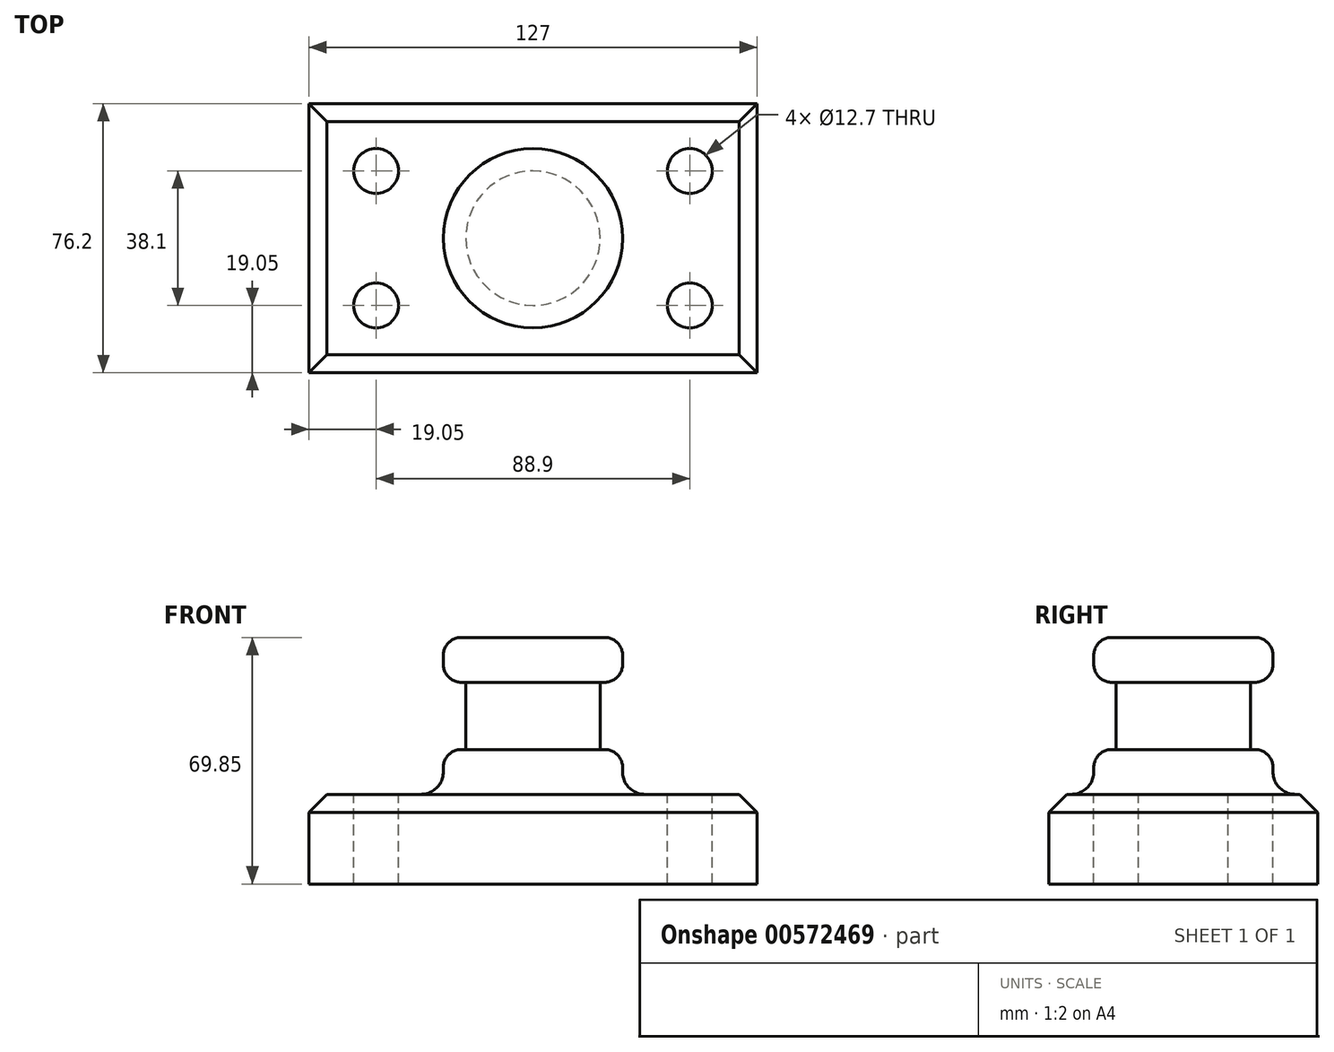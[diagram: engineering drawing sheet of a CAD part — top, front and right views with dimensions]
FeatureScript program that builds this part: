
annotation { "Feature Type Name" : "Feature", "Feature Type Description" : "" }
export const myFeature = defineFeature(function(context is Context, id is Id, definition is map)
    precondition{}
    {
        {
            var Q0;
            Q0=qCreatedBy(makeId("Top.planeOp"),FACE);
            var sketch = newSketch(context, id + "F0", { "sketchPlane" : qUnion([Q0])});
            skLineSegment(sketch, "E0.bottom", {"start": v(-63.5, 38.1) * mm, "end": v(63.5, 38.1) * mm});
            skLineSegment(sketch, "E0.top", {"start": v(-63.5, -38.1) * mm, "end": v(63.5, -38.1) * mm});
            skLineSegment(sketch, "E0.left", {"start": v(-63.5, 38.1) * mm, "end": v(-63.5, -38.1) * mm});
            skLineSegment(sketch, "E0.right", {"start": v(63.5, 38.1) * mm, "end": v(63.5, -38.1) * mm});
            skPoint(sketch, "E0.middle", {"position": v(0, 0) * mm});
            skLineSegment(sketch, "E1.bottom", {"start": v(-63.05, 38.1) * mm, "end": v(-63.76, 38.1) * mm});
            skLineSegment(sketch, "E1.top", {"start": v(-63.05, 38.1) * mm, "end": v(-63.76, 38.1) * mm});
            skLineSegment(sketch, "E1.left", {"start": v(-63.05, 38.1) * mm, "end": v(-63.05, 38.1) * mm});
            skLineSegment(sketch, "E1.right", {"start": v(-63.76, 38.1) * mm, "end": v(-63.76, 38.1) * mm});
            skPoint(sketch, "E1.middle", {"position": v(-63.4, 38.1) * mm});
            skSolve(sketch);
        }
        {
            var Q0;
            {var subQ1=sQuery(id+"F0.wireOp",EDGE,"E0.bottom");Q0=makeQuery(id+"F0.imprint","IMPRINT",FACE,{"disambiguationData":[TD([[makeQuery(id+"F0.imprint","IMPRINT",EDGE,{"derivedFrom":subQ1}),-1.0]])]});}
            extrude(context, id + "F1", {"entities" : qUnion([Q0]), "depth" : 25.4 * mm, "offsetDistance" : 25.4 * mm});
        }
        {
            var Q0;
            Q0=makeQuery(id+"F1.opExtrude","CAP_FACE",FACE,{"disambiguationData":[OSD([sQuery(id+"F0.wireOp",EDGE,"E0.bottom"),sQuery(id+"F0.wireOp",EDGE,"E0.top"),sQuery(id+"F0.wireOp",EDGE,"E0.left"),sQuery(id+"F0.wireOp",EDGE,"E0.right"),sQuery(id+"F0.wireOp",EDGE,"E1.top")])],"isStart":false});
            var sketch = newSketch(context, id + "F2", { "sketchPlane" : qUnion([Q0])});
            skCircle(sketch, "E2", {"center": v(-44.45, 19.05) * mm, "radius": 6.35 * mm});
            skCircle(sketch, "E3", {"center": v(-44.45, -19.05) * mm, "radius": 6.35 * mm});
            skCircle(sketch, "E4", {"center": v(44.45, 19.05) * mm, "radius": 6.35 * mm});
            skCircle(sketch, "E5", {"center": v(44.45, -19.05) * mm, "radius": 6.35 * mm});
            skSolve(sketch);
        }
        {
            var Q0;
            Q0=makeQuery(id+"F2.imprint","IMPRINT",FACE,{"disambiguationData":[TD([[makeQuery(id+"F2.imprint","IMPRINT",EDGE,{"derivedFrom":sQuery(id+"F2.wireOp",EDGE,"E2")}),1.0]])]});
            var Q1;
            Q1=makeQuery(id+"F2.imprint","IMPRINT",FACE,{"disambiguationData":[TD([[makeQuery(id+"F2.imprint","IMPRINT",EDGE,{"derivedFrom":sQuery(id+"F2.wireOp",EDGE,"E3")}),1.0]])]});
            var Q2;
            Q2=makeQuery(id+"F2.imprint","IMPRINT",FACE,{"disambiguationData":[TD([[makeQuery(id+"F2.imprint","IMPRINT",EDGE,{"derivedFrom":sQuery(id+"F2.wireOp",EDGE,"E4")}),1.0]])]});
            var Q3;
            Q3=makeQuery(id+"F2.imprint","IMPRINT",FACE,{"disambiguationData":[TD([[makeQuery(id+"F2.imprint","IMPRINT",EDGE,{"derivedFrom":sQuery(id+"F2.wireOp",EDGE,"E5")}),1.0]])]});
            extrude(context, id + "F3", {"entities" : qUnion([Q0, Q1, Q2, Q3]), "operationType" : NewBodyOperationType.REMOVE, "oppositeDirection" : true, "depth" : 25.4 * mm, "offsetDistance" : 25.4 * mm});
        }
        {
            var Q0;
            Q0=qCreatedBy(makeId("Front.planeOp"),FACE);
            var sketch = newSketch(context, id + "F4", { "sketchPlane" : qUnion([Q0])});
            skLineSegment(sketch, "E6.bottom", {"start": v(0, 26.27) * mm, "end": v(0, 26.27) * mm});
            skLineSegment(sketch, "E7.bottom", {"start": v(0, 38.1) * mm, "end": v(25.4, 38.1) * mm});
            skLineSegment(sketch, "E7.top", {"start": v(0, 25.4) * mm, "end": v(25.4, 25.4) * mm});
            skLineSegment(sketch, "E7.left", {"start": v(0, 38.1) * mm, "end": v(0, 25.4) * mm});
            skLineSegment(sketch, "E7.right", {"start": v(25.4, 38.1) * mm, "end": v(25.4, 25.4) * mm});
            skSolve(sketch);
        }
        {
            var Q0;
            Q0=makeQuery(id+"F4.imprint","IMPRINT",FACE,{"disambiguationData":[TD([[makeQuery(id+"F4.imprint","IMPRINT",EDGE,{"derivedFrom":sQuery(id+"F4.wireOp",EDGE,"E7.bottom")}),-1.0]])]});
            var Q1;
            Q1=sQuery(id+"F4.wireOp",EDGE,"E7.left");
            revolve(context, id + "F5", {"operationType" : NewBodyOperationType.ADD, "entities" : qUnion([Q0]), "axis" : qUnion([Q1]), "revolveType" : RevolveType.FULL});
        }
        {
            var Q0;
            Q0=qCreatedBy(makeId("Front.planeOp"),FACE);
            var sketch = newSketch(context, id + "F6", { "sketchPlane" : qUnion([Q0])});
            skLineSegment(sketch, "E8.bottom", {"start": v(0, 38.1) * mm, "end": v(19.05, 38.1) * mm});
            skLineSegment(sketch, "E8.top", {"start": v(0, 57.15) * mm, "end": v(19.05, 57.15) * mm});
            skLineSegment(sketch, "E8.left", {"start": v(0, 38.1) * mm, "end": v(0, 57.15) * mm});
            skLineSegment(sketch, "E8.right", {"start": v(19.05, 38.1) * mm, "end": v(19.05, 57.15) * mm});
            skSolve(sketch);
        }
        {
            var Q0;
            Q0=makeQuery(id+"F6.imprint","IMPRINT",FACE,{"disambiguationData":[TD([[makeQuery(id+"F6.imprint","IMPRINT",EDGE,{"derivedFrom":sQuery(id+"F6.wireOp",EDGE,"E8.bottom")}),1.0]])]});
            var Q1;
            Q1=sQuery(id+"F6.wireOp",EDGE,"E8.left");
            revolve(context, id + "F7", {"operationType" : NewBodyOperationType.ADD, "entities" : qUnion([Q0]), "axis" : qUnion([Q1]), "revolveType" : RevolveType.FULL});
        }
        {
            var Q0;
            Q0=qCreatedBy(makeId("Front.planeOp"),FACE);
            var sketch = newSketch(context, id + "F8", { "sketchPlane" : qUnion([Q0])});
            skLineSegment(sketch, "E9.bottom", {"start": v(0, 57.15) * mm, "end": v(25.4, 57.15) * mm});
            skLineSegment(sketch, "E9.top", {"start": v(0, 69.85) * mm, "end": v(25.4, 69.85) * mm});
            skLineSegment(sketch, "E9.left", {"start": v(0, 57.15) * mm, "end": v(0, 69.85) * mm});
            skLineSegment(sketch, "E9.right", {"start": v(25.4, 57.15) * mm, "end": v(25.4, 69.85) * mm});
            skSolve(sketch);
        }
        {
            var Q0;
            Q0=makeQuery(id+"F8.imprint","IMPRINT",FACE,{"disambiguationData":[TD([[makeQuery(id+"F8.imprint","IMPRINT",EDGE,{"derivedFrom":sQuery(id+"F8.wireOp",EDGE,"E9.bottom")}),1.0]])]});
            var Q1;
            Q1=sQuery(id+"F8.wireOp",EDGE,"E9.left");
            revolve(context, id + "F9", {"operationType" : NewBodyOperationType.ADD, "entities" : qUnion([Q0]), "axis" : qUnion([Q1]), "revolveType" : RevolveType.FULL});
        }
        {
            var Q0;
            Q0=makeQuery(id+"F5.opRevolve","SWEPT_EDGE",EDGE,{"disambiguationData":[OSD([sQuery(id+"F4.wireOp",EDGE,"E7.bottom"),sQuery(id+"F4.wireOp",EDGE,"E7.right")])]});
            var Q1;
            Q1=makeQuery(id+"F9.opRevolve","SWEPT_EDGE",EDGE,{"disambiguationData":[OSD([sQuery(id+"F8.wireOp",EDGE,"E9.bottom"),sQuery(id+"F8.wireOp",EDGE,"E9.right")])]});
            var Q2;
            Q2=makeQuery(id+"F7.opRevolve","SWEPT_EDGE",EDGE,{"disambiguationData":[OSD([sQuery(id+"F6.wireOp",EDGE,"E8.bottom"),sQuery(id+"F6.wireOp",EDGE,"E8.right")])]});
            var Q3;
            Q3=makeQuery(id+"F9.opRevolve","SWEPT_EDGE",EDGE,{"disambiguationData":[OSD([sQuery(id+"F8.wireOp",EDGE,"E9.top"),sQuery(id+"F8.wireOp",EDGE,"E9.right")])]});
            fillet(context, id + "F10", {"entities" : qUnion([Q0, Q1, Q2, Q3]), "radius" : 5.08 * mm, "tangentPropagation" : true, "allowEdgeOverflow" : false});
        }
        {
            var Q0;
            Q0=makeQuery(id+"F9.opRevolve","SWEPT_EDGE",EDGE,{"disambiguationData":[OSD([sQuery(id+"F8.wireOp",EDGE,"E9.top"),sQuery(id+"F8.wireOp",EDGE,"E9.right")])]});
            var Q1;
            Q1=makeQuery(id+"F5.opRevolve","SWEPT_EDGE",EDGE,{"disambiguationData":[OSD([sQuery(id+"F4.wireOp",EDGE,"E7.bottom"),sQuery(id+"F4.wireOp",EDGE,"E7.right")])]});
            var Q2;
            Q2=makeQuery(id+"F9.opRevolve","SWEPT_EDGE",EDGE,{"disambiguationData":[OSD([sQuery(id+"F8.wireOp",EDGE,"E9.bottom"),sQuery(id+"F8.wireOp",EDGE,"E9.right")])]});
            var Q3;
            Q3=makeQuery(id+"F5.opRevolve","SWEPT_FACE",FACE,{"disambiguationData":[OSD([sQuery(id+"F4.wireOp",EDGE,"E7.right")])]});
            fillet(context, id + "F11", {"entities" : qUnion([Q0, Q1, Q2, Q3]), "radius" : 6.35 * mm, "tangentPropagation" : true, "allowEdgeOverflow" : false});
        }
        {
            var Q0;
            Q0=makeQuery(id+"F1.opExtrude","CAP_EDGE",EDGE,{"disambiguationData":[OSD([sQuery(id+"F0.wireOp",EDGE,"E0.left")])],"isStart":false});
            var Q1;
            Q1=makeQuery(id+"F1.opExtrude","CAP_EDGE",EDGE,{"disambiguationData":[OSD([sQuery(id+"F0.wireOp",EDGE,"E0.bottom"),sQuery(id+"F0.wireOp",EDGE,"E1.top")])],"isStart":false});
            var Q2;
            Q2=makeQuery(id+"F1.opExtrude","CAP_EDGE",EDGE,{"disambiguationData":[OSD([sQuery(id+"F0.wireOp",EDGE,"E0.top")])],"isStart":false});
            var Q3;
            Q3=makeQuery(id+"F1.opExtrude","CAP_EDGE",EDGE,{"disambiguationData":[OSD([sQuery(id+"F0.wireOp",EDGE,"E0.right")])],"isStart":false});
            chamfer(context, id + "F12", {"entities" : qUnion([Q0, Q1, Q2, Q3]), "width" : 5.08 * mm, "tangentPropagation" : true});
        }
    });
